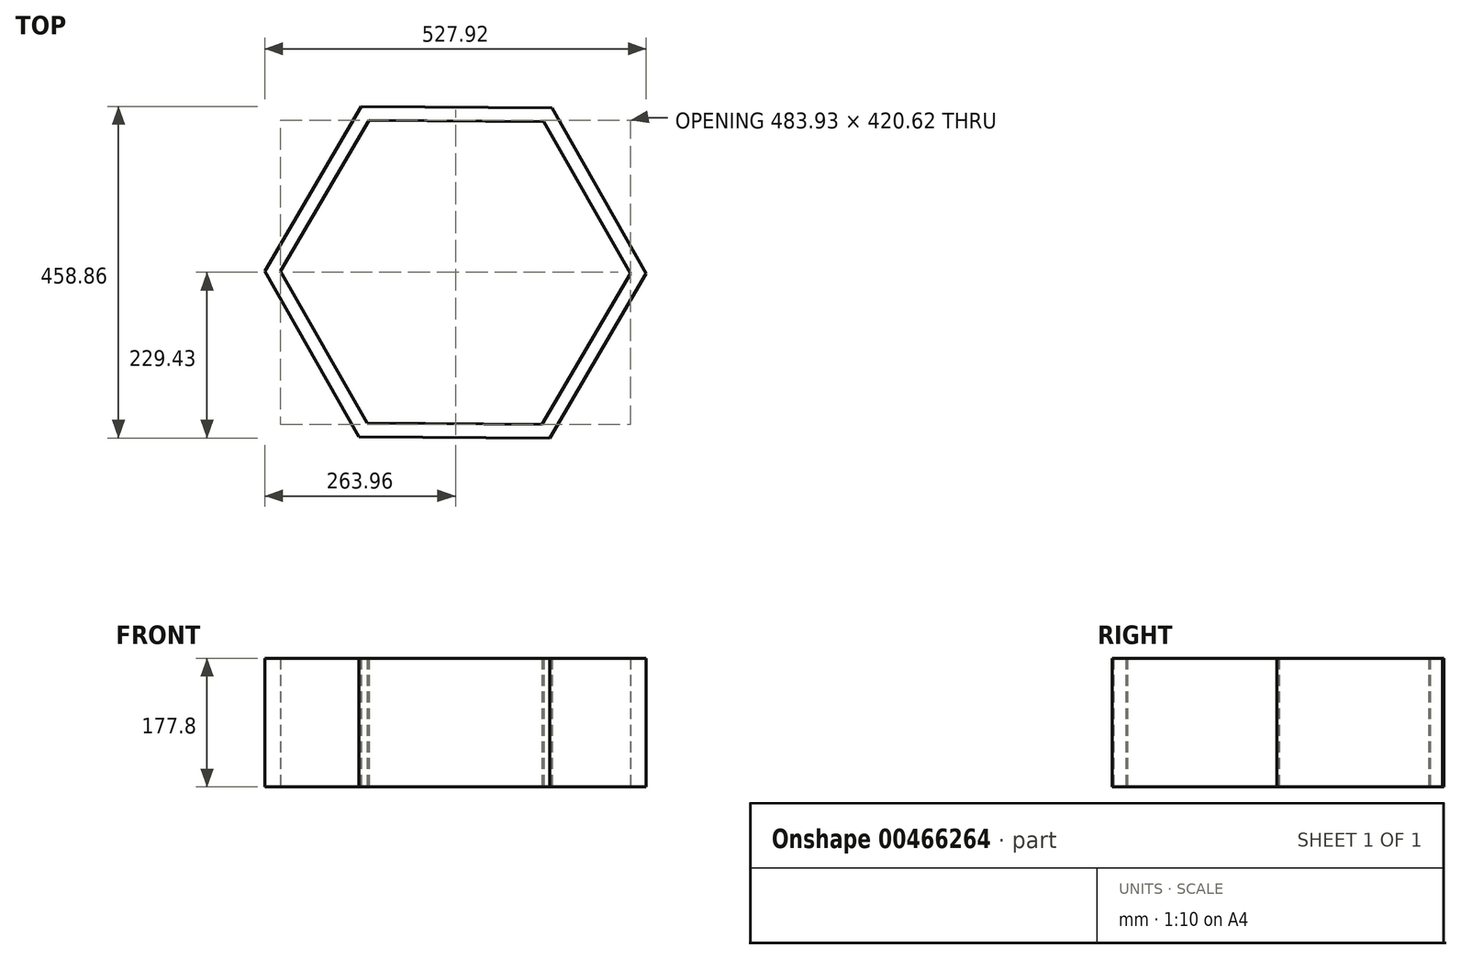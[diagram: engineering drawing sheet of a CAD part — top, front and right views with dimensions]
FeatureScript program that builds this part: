
annotation { "Feature Type Name" : "Feature", "Feature Type Description" : "" }
export const myFeature = defineFeature(function(context is Context, id is Id, definition is map)
    precondition{}
    {
        {
            var Q0;
            Q0=qCreatedBy(makeId("Top.planeOp"),FACE);
            var sketch = newSketch(context, id + "F0", { "sketchPlane" : qUnion([Q0])});
            skCircle(sketch, "E0.cCircle", {"center": v(0, 0) * mm, "radius": 209.55 * mm, "construction": true});
            skLineSegment(sketch, "E0.0", {"start": v(122.3, 208.78) * mm, "end": v(241.96, -1.53) * mm});
            skLineSegment(sketch, "E0.1", {"start": v(241.96, -1.53) * mm, "end": v(119.66, -210.3) * mm});
            skLineSegment(sketch, "E0.2", {"start": v(119.66, -210.3) * mm, "end": v(-122.3, -208.78) * mm});
            skLineSegment(sketch, "E0.3", {"start": v(-122.3, -208.78) * mm, "end": v(-241.96, 1.53) * mm});
            skLineSegment(sketch, "E0.4", {"start": v(-241.96, 1.53) * mm, "end": v(-119.66, 210.3) * mm});
            skLineSegment(sketch, "E0.5", {"start": v(-119.66, 210.3) * mm, "end": v(122.3, 208.78) * mm});
            skPoint(sketch, "E0.0.midPoint", {"position": v(182.13, 103.63) * mm});
            skLineSegment(sketch, "E1.0", {"start": v(-133.42, -227.76) * mm, "end": v(-263.96, 1.67) * mm});
            skLineSegment(sketch, "E1.1", {"start": v(-130.54, 229.43) * mm, "end": v(133.42, 227.76) * mm});
            skLineSegment(sketch, "E1.2", {"start": v(133.42, 227.76) * mm, "end": v(263.96, -1.67) * mm});
            skLineSegment(sketch, "E1.3", {"start": v(-263.96, 1.67) * mm, "end": v(-130.54, 229.43) * mm});
            skLineSegment(sketch, "E1.4", {"start": v(263.96, -1.67) * mm, "end": v(130.54, -229.43) * mm});
            skLineSegment(sketch, "E1.5", {"start": v(130.54, -229.43) * mm, "end": v(-133.42, -227.76) * mm});
            skLineSegment(sketch, "E2", {"start": v(-130.54, 229.43) * mm, "end": v(-119.66, 210.3) * mm, "construction": true});
            skSolve(sketch);
        }
        {
            var Q0;
            Q0 = qSketchRegion(id + "F0", true);
            extrude(context, id + "F1", {"entities" : qUnion([Q0]), "depth" : 177.8 * mm});
        }
    });
